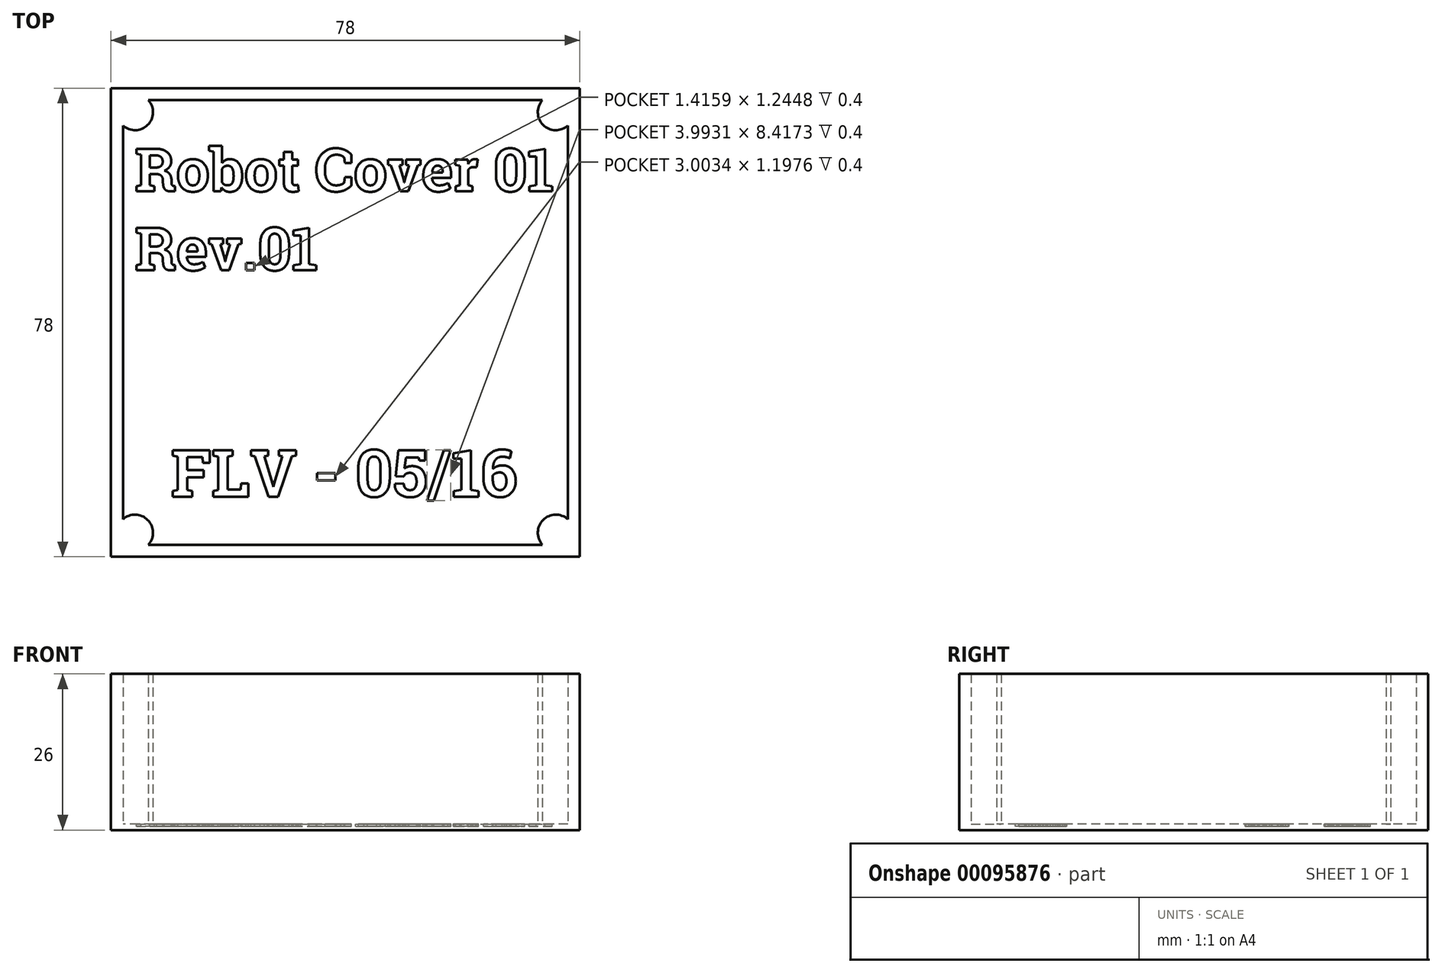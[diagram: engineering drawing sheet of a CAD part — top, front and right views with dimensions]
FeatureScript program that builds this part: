
annotation { "Feature Type Name" : "Feature", "Feature Type Description" : "" }
export const myFeature = defineFeature(function(context is Context, id is Id, definition is map)
    precondition{}
    {
        {
            var Q0;
            Q0=qCreatedBy(makeId("Top.planeOp"),FACE);
            var sketch = newSketch(context, id + "F0", { "sketchPlane" : qUnion([Q0])});
            skLineSegment(sketch, "E0.bottom", {"start": v(-28, 33) * mm, "end": v(50, 33) * mm});
            skLineSegment(sketch, "E0.top", {"start": v(-28, -45) * mm, "end": v(50, -45) * mm});
            skLineSegment(sketch, "E0.left", {"start": v(-28, 33) * mm, "end": v(-28, -45) * mm});
            skLineSegment(sketch, "E0.right", {"start": v(50, 33) * mm, "end": v(50, -45) * mm});
            skLineSegment(sketch, "E1.bottom", {"start": v(-28, -35) * mm, "end": v(-31, -35) * mm});
            skLineSegment(sketch, "E1.top", {"start": v(-28, -29) * mm, "end": v(-31, -29) * mm});
            skLineSegment(sketch, "E1.left", {"start": v(-28, -35) * mm, "end": v(-28, -29) * mm});
            skLineSegment(sketch, "E1.right", {"start": v(-31, -35) * mm, "end": v(-31, -29) * mm});
            skLineSegment(sketch, "E2.0.1.0", {"start": v(-28, -25) * mm, "end": v(-31, -25) * mm});
            skLineSegment(sketch, "E2.0.1.1", {"start": v(-28, -19) * mm, "end": v(-31, -19) * mm});
            skLineSegment(sketch, "E2.0.1.2", {"start": v(-31, -25) * mm, "end": v(-31, -19) * mm});
            skLineSegment(sketch, "E2.0.1.3", {"start": v(-28, -25) * mm, "end": v(-28, -19) * mm});
            skLineSegment(sketch, "E2.0.2.0", {"start": v(-28, -15) * mm, "end": v(-31, -15) * mm});
            skLineSegment(sketch, "E2.0.2.1", {"start": v(-28, -9) * mm, "end": v(-31, -9) * mm});
            skLineSegment(sketch, "E2.0.2.2", {"start": v(-31, -15) * mm, "end": v(-31, -9) * mm});
            skLineSegment(sketch, "E2.0.2.3", {"start": v(-28, -15) * mm, "end": v(-28, -9) * mm});
            skLineSegment(sketch, "E2.0.3.0", {"start": v(-28, -5) * mm, "end": v(-31, -5) * mm});
            skLineSegment(sketch, "E2.0.3.1", {"start": v(-28, 1) * mm, "end": v(-31, 1) * mm});
            skLineSegment(sketch, "E2.0.3.2", {"start": v(-31, -5) * mm, "end": v(-31, 1) * mm});
            skLineSegment(sketch, "E2.0.3.3", {"start": v(-28, -5) * mm, "end": v(-28, 1) * mm});
            skLineSegment(sketch, "E2.0.4.0", {"start": v(-28, 5) * mm, "end": v(-31, 5) * mm});
            skLineSegment(sketch, "E2.0.4.1", {"start": v(-28, 11) * mm, "end": v(-31, 11) * mm});
            skLineSegment(sketch, "E2.0.4.2", {"start": v(-31, 5) * mm, "end": v(-31, 11) * mm});
            skLineSegment(sketch, "E2.0.4.3", {"start": v(-28, 5) * mm, "end": v(-28, 11) * mm});
            skLineSegment(sketch, "E2.0.5.0", {"start": v(-28, 15) * mm, "end": v(-31, 15) * mm});
            skLineSegment(sketch, "E2.0.5.1", {"start": v(-28, 21) * mm, "end": v(-31, 21) * mm});
            skLineSegment(sketch, "E2.0.5.2", {"start": v(-31, 15) * mm, "end": v(-31, 21) * mm});
            skLineSegment(sketch, "E2.0.5.3", {"start": v(-28, 15) * mm, "end": v(-28, 21) * mm});
            skLineSegment(sketch, "E2.direction1", {"start": v(-31, -35) * mm, "end": v(-6, -35) * mm, "construction": true});
            skLineSegment(sketch, "E2.direction2", {"start": v(-31, -35) * mm, "end": v(-31, -25) * mm, "construction": true});
            skLineSegment(sketch, "E3.bottom", {"start": v(50, -35) * mm, "end": v(53, -35) * mm});
            skLineSegment(sketch, "E3.top", {"start": v(50, -29) * mm, "end": v(53, -29) * mm});
            skLineSegment(sketch, "E3.left", {"start": v(50, -35) * mm, "end": v(50, -29) * mm});
            skLineSegment(sketch, "E3.right", {"start": v(53, -35) * mm, "end": v(53, -29) * mm});
            skLineSegment(sketch, "E4.0.1.0", {"start": v(50, -25) * mm, "end": v(50, -19) * mm});
            skLineSegment(sketch, "E4.0.1.1", {"start": v(50, -19) * mm, "end": v(53, -19) * mm});
            skLineSegment(sketch, "E4.0.1.2", {"start": v(53, -25) * mm, "end": v(53, -19) * mm});
            skLineSegment(sketch, "E4.0.1.3", {"start": v(50, -25) * mm, "end": v(53, -25) * mm});
            skLineSegment(sketch, "E4.0.2.0", {"start": v(50, -15) * mm, "end": v(50, -9) * mm});
            skLineSegment(sketch, "E4.0.2.1", {"start": v(50, -9) * mm, "end": v(53, -9) * mm});
            skLineSegment(sketch, "E4.0.2.2", {"start": v(53, -15) * mm, "end": v(53, -9) * mm});
            skLineSegment(sketch, "E4.0.2.3", {"start": v(50, -15) * mm, "end": v(53, -15) * mm});
            skLineSegment(sketch, "E4.0.3.0", {"start": v(50, -5) * mm, "end": v(50, 1) * mm});
            skLineSegment(sketch, "E4.0.3.1", {"start": v(50, 1) * mm, "end": v(53, 1) * mm});
            skLineSegment(sketch, "E4.0.3.2", {"start": v(53, -5) * mm, "end": v(53, 1) * mm});
            skLineSegment(sketch, "E4.0.3.3", {"start": v(50, -5) * mm, "end": v(53, -5) * mm});
            skLineSegment(sketch, "E4.0.4.0", {"start": v(50, 5) * mm, "end": v(50, 11) * mm});
            skLineSegment(sketch, "E4.0.4.1", {"start": v(50, 11) * mm, "end": v(53, 11) * mm});
            skLineSegment(sketch, "E4.0.4.2", {"start": v(53, 5) * mm, "end": v(53, 11) * mm});
            skLineSegment(sketch, "E4.0.4.3", {"start": v(50, 5) * mm, "end": v(53, 5) * mm});
            skLineSegment(sketch, "E4.0.5.0", {"start": v(50, 15) * mm, "end": v(50, 21) * mm});
            skLineSegment(sketch, "E4.0.5.1", {"start": v(50, 21) * mm, "end": v(53, 21) * mm});
            skLineSegment(sketch, "E4.0.5.2", {"start": v(53, 15) * mm, "end": v(53, 21) * mm});
            skLineSegment(sketch, "E4.0.5.3", {"start": v(50, 15) * mm, "end": v(53, 15) * mm});
            skLineSegment(sketch, "E4.direction1", {"start": v(50, -35) * mm, "end": v(73.5, -35) * mm, "construction": true});
            skLineSegment(sketch, "E4.direction2", {"start": v(50, -35) * mm, "end": v(50, -25) * mm, "construction": true});
            skSolve(sketch);
        }
        {
            var Q0;
            {var subQ14=sQuery(id+"F0.wireOp",EDGE,"E0.bottom");Q0=makeQuery(id+"F0.imprint","IMPRINT",FACE,{"disambiguationData":[TD([[makeQuery(id+"F0.imprint","IMPRINT",EDGE,{"derivedFrom":subQ14}),-1.0]])]});}
            extrude(context, id + "F1", {"entities" : qUnion([Q0]), "depth" : 1 * mm});
        }
        {
            var Q0;
            Q0=makeQuery(id+"F1.opExtrude","CAP_FACE",FACE,{"disambiguationData":[OSD([sQuery(id+"F0.wireOp",EDGE,"E0.bottom"),sQuery(id+"F0.wireOp",EDGE,"E0.top"),sQuery(id+"F0.wireOp",EDGE,"E0.left"),sQuery(id+"F0.wireOp",EDGE,"E0.right"),sQuery(id+"F0.wireOp",EDGE,"E1.left"),sQuery(id+"F0.wireOp",EDGE,"E2.0.1.3"),sQuery(id+"F0.wireOp",EDGE,"E2.0.2.3"),sQuery(id+"F0.wireOp",EDGE,"E2.0.3.3"),sQuery(id+"F0.wireOp",EDGE,"E2.0.4.3"),sQuery(id+"F0.wireOp",EDGE,"E2.0.5.3"),sQuery(id+"F0.wireOp",EDGE,"E3.left"),sQuery(id+"F0.wireOp",EDGE,"E4.0.1.0"),sQuery(id+"F0.wireOp",EDGE,"E4.0.2.0"),sQuery(id+"F0.wireOp",EDGE,"E4.0.3.0"),sQuery(id+"F0.wireOp",EDGE,"E4.0.4.0"),sQuery(id+"F0.wireOp",EDGE,"E4.0.5.0")])],"isStart":false});
            var sketch = newSketch(context, id + "F2", { "sketchPlane" : qUnion([Q0])});
            skText(sketch, "E5", { "text": "Robot Cover 01\nRev.01", "fontName": "RobotoSlab-Bold.ttf"});
            skText(sketch, "E6", { "text": "FLV - 05/16\n", "fontName": "RobotoSlab-Bold.ttf"});
            const initialGuessF2  = {"E5": [-0.024, 0.01583, 1, 0, 0.00717], "E6": [-0.018, -0.035, 1, 0, 0.00785]};
            skSetInitialGuess(sketch, initialGuessF2);
            skSolve(sketch);
        }
        {
            var Q0;
            Q0 = qSketchRegion(id + "F2", true);
            extrude(context, id + "F3", {"entities" : qUnion([Q0]), "operationType" : NewBodyOperationType.REMOVE, "oppositeDirection" : true, "depth" : 0.4 * mm});
        }
        {
            var Q0;
            {var subQ0=sQuery(id+"F0.wireOp",EDGE,"E0.top");var subQ1=sQuery(id+"F0.wireOp",EDGE,"E4.0.5.0");var subQ2=sQuery(id+"F0.wireOp",EDGE,"E4.0.4.0");var subQ3=sQuery(id+"F0.wireOp",EDGE,"E4.0.3.0");var subQ4=sQuery(id+"F0.wireOp",EDGE,"E4.0.2.0");var subQ5=sQuery(id+"F0.wireOp",EDGE,"E4.0.1.0");var subQ6=sQuery(id+"F0.wireOp",EDGE,"E3.left");var subQ7=sQuery(id+"F0.wireOp",EDGE,"E0.right");var subQ8=sQuery(id+"F0.wireOp",EDGE,"E0.bottom");var subQ9=sQuery(id+"F0.wireOp",EDGE,"E2.0.5.3");var subQ10=sQuery(id+"F0.wireOp",EDGE,"E2.0.4.3");var subQ11=sQuery(id+"F0.wireOp",EDGE,"E2.0.3.3");var subQ12=sQuery(id+"F0.wireOp",EDGE,"E2.0.2.3");var subQ13=sQuery(id+"F0.wireOp",EDGE,"E2.0.1.3");var subQ14=sQuery(id+"F0.wireOp",EDGE,"E1.left");var subQ15=sQuery(id+"F0.wireOp",EDGE,"E0.left");Q0=makeQuery(id+"F3.boolean.opBoolean","SPLIT",FACE,{"disambiguationData":[TD([makeQuery(id+"F1.opExtrude","SWEPT_FACE",FACE,{"disambiguationData":[OSD([subQ8])]})])],"derivedFrom":makeQuery(id+"F1.opExtrude","CAP_FACE",FACE,{"disambiguationData":[OSD([subQ8,subQ0,subQ15,subQ7,subQ14,subQ13,subQ12,subQ11,subQ10,subQ9,subQ6,subQ5,subQ4,subQ3,subQ2,subQ1])],"isStart":false})});}
            var sketch = newSketch(context, id + "F4", { "sketchPlane" : qUnion([Q0])});
            skLineSegment(sketch, "E7.bottom", {"start": v(-28, 33) * mm, "end": v(50, 33) * mm});
            skLineSegment(sketch, "E7.top", {"start": v(-28, -45) * mm, "end": v(50, -45) * mm});
            skLineSegment(sketch, "E7.left", {"start": v(-28, 33) * mm, "end": v(-28, -45) * mm});
            skLineSegment(sketch, "E7.right", {"start": v(50, 33) * mm, "end": v(50, -45) * mm});
            skLineSegment(sketch, "E8.bottom", {"start": v(-26, 31) * mm, "end": v(48, 31) * mm});
            skLineSegment(sketch, "E8.top", {"start": v(-26, -43) * mm, "end": v(48, -43) * mm});
            skLineSegment(sketch, "E8.left", {"start": v(-26, 31) * mm, "end": v(-26, -43) * mm});
            skLineSegment(sketch, "E8.right", {"start": v(48, 31) * mm, "end": v(48, -43) * mm});
            skSolve(sketch);
        }
        {
            var Q0;
            Q0 = qSketchRegion(id + "F4", true);
            extrude(context, id + "F5", {"entities" : qUnion([Q0]), "operationType" : NewBodyOperationType.ADD, "depth" : 25 * mm});
        }
        {
            var Q0;
            {var subQ0=sQuery(id+"F0.wireOp",EDGE,"E0.top");var subQ1=sQuery(id+"F0.wireOp",EDGE,"E4.0.5.0");var subQ2=sQuery(id+"F0.wireOp",EDGE,"E4.0.4.0");var subQ3=sQuery(id+"F0.wireOp",EDGE,"E4.0.3.0");var subQ4=sQuery(id+"F0.wireOp",EDGE,"E4.0.2.0");var subQ5=sQuery(id+"F0.wireOp",EDGE,"E4.0.1.0");var subQ6=sQuery(id+"F0.wireOp",EDGE,"E3.left");var subQ7=sQuery(id+"F0.wireOp",EDGE,"E0.right");var subQ8=sQuery(id+"F0.wireOp",EDGE,"E0.bottom");var subQ9=sQuery(id+"F0.wireOp",EDGE,"E2.0.5.3");var subQ10=sQuery(id+"F0.wireOp",EDGE,"E2.0.4.3");var subQ11=sQuery(id+"F0.wireOp",EDGE,"E2.0.3.3");var subQ12=sQuery(id+"F0.wireOp",EDGE,"E2.0.2.3");var subQ13=sQuery(id+"F0.wireOp",EDGE,"E2.0.1.3");var subQ14=sQuery(id+"F0.wireOp",EDGE,"E1.left");var subQ15=sQuery(id+"F0.wireOp",EDGE,"E0.left");Q0=makeQuery(id+"F3.boolean.opBoolean","SPLIT",FACE,{"disambiguationData":[TD([makeQuery(id+"F1.opExtrude","SWEPT_FACE",FACE,{"disambiguationData":[OSD([subQ8])]})])],"derivedFrom":makeQuery(id+"F1.opExtrude","CAP_FACE",FACE,{"disambiguationData":[OSD([subQ8,subQ0,subQ15,subQ7,subQ14,subQ13,subQ12,subQ11,subQ10,subQ9,subQ6,subQ5,subQ4,subQ3,subQ2,subQ1])],"isStart":false})});}
            var sketch = newSketch(context, id + "F6", { "sketchPlane" : qUnion([Q0])});
            skCircle(sketch, "E9", {"center": v(-24, 29) * mm, "radius": 3 * mm});
            skCircle(sketch, "E10", {"center": v(46, 29) * mm, "radius": 3 * mm});
            skCircle(sketch, "E11", {"center": v(46, -41) * mm, "radius": 3 * mm});
            skCircle(sketch, "E12", {"center": v(-24, -41) * mm, "radius": 3 * mm});
            skSolve(sketch);
        }
        {
            var Q0;
            Q0 = qSketchRegion(id + "F6", true);
            extrude(context, id + "F7", {"entities" : qUnion([Q0]), "operationType" : NewBodyOperationType.ADD, "depth" : 25 * mm});
        }
    });
